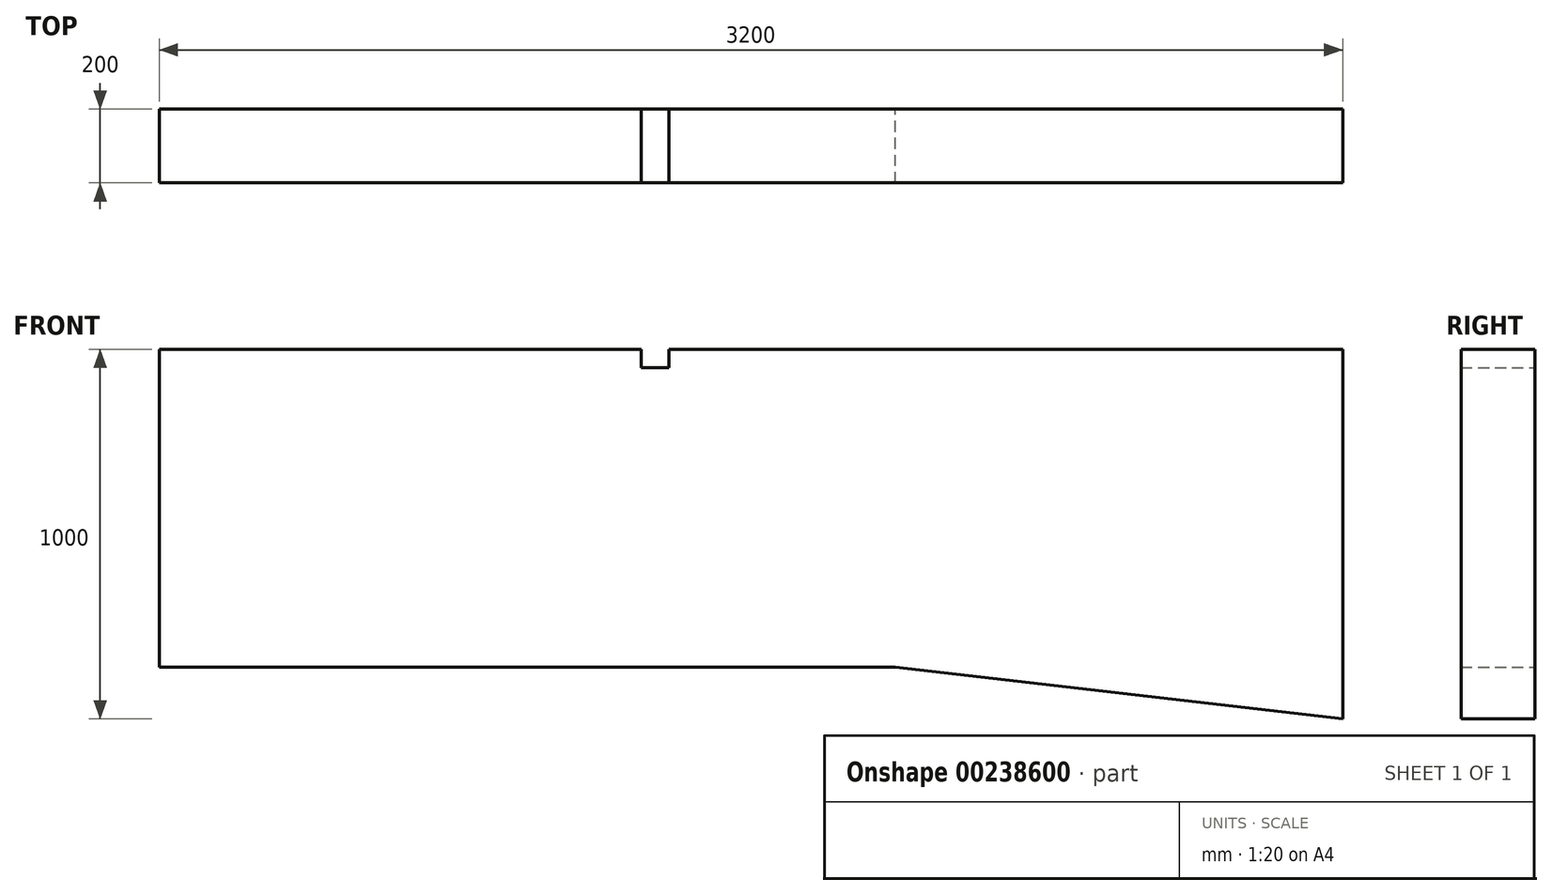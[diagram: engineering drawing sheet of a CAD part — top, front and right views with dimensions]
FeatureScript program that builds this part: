
annotation { "Feature Type Name" : "Feature", "Feature Type Description" : "" }
export const myFeature = defineFeature(function(context is Context, id is Id, definition is map)
    precondition{}
    {
        {
            var Q0;
            Q0=qCreatedBy(makeId("Front.planeOp"),FACE);
            var sketch = newSketch(context, id + "F0", { "sketchPlane" : qUnion([Q0])});
            skLineSegment(sketch, "E0.bottom", {"start": v(0, 0) * mm, "end": v(-3200, 0) * mm});
            skLineSegment(sketch, "E0.top", {"start": v(0, 860) * mm, "end": v(-3200, 860) * mm});
            skLineSegment(sketch, "E0.left", {"start": v(0, 0) * mm, "end": v(0, 860) * mm});
            skLineSegment(sketch, "E0.right", {"start": v(-3200, 0) * mm, "end": v(-3200, 860) * mm});
            skSolve(sketch);
        }
        {
            var Q0;
            Q0=makeQuery(id+"F0.imprint","IMPRINT",FACE,{"disambiguationData":[TD([[makeQuery(id+"F0.imprint","IMPRINT",EDGE,{"derivedFrom":sQuery(id+"F0.wireOp",EDGE,"E0.bottom")}),-1.0]])]});
            extrude(context, id + "F1", {"entities" : qUnion([Q0]), "depth" : 200 * mm});
        }
        {
            var Q0;
            Q0=qCreatedBy(makeId("Front.planeOp"),FACE);
            var sketch = newSketch(context, id + "F2", { "sketchPlane" : qUnion([Q0])});
            skLineSegment(sketch, "E1", {"start": v(0, 0) * mm, "end": v(0, -140) * mm});
            skLineSegment(sketch, "E2", {"start": v(0, -140) * mm, "end": v(-1210, 0) * mm});
            skLineSegment(sketch, "E3", {"start": v(-1210, 0) * mm, "end": v(0, 0) * mm});
            skSolve(sketch);
        }
        {
            var Q0;
            Q0=makeQuery(id+"F2.imprint","IMPRINT",FACE,{"disambiguationData":[TD([[makeQuery(id+"F2.imprint","IMPRINT",EDGE,{"derivedFrom":sQuery(id+"F2.wireOp",EDGE,"E1")}),-1.0]])]});
            var Q1;
            Q1=makeQuery(id+"F1.opExtrude","CAP_FACE",FACE,{"disambiguationData":[OSD([sQuery(id+"F0.wireOp",EDGE,"E0.bottom"),sQuery(id+"F0.wireOp",EDGE,"E0.top"),sQuery(id+"F0.wireOp",EDGE,"E0.left"),sQuery(id+"F0.wireOp",EDGE,"E0.right")])],"isStart":false});
            extrude(context, id + "F3", {"entities" : qUnion([Q0]), "operationType" : NewBodyOperationType.ADD, "endBound" : BoundingType.UP_TO_SURFACE, "endBoundEntityFace" : qUnion([Q1]), "depth" : 25 * mm});
        }
        {
            var Q0;
            Q0=qCreatedBy(makeId("Front.planeOp"),FACE);
            var sketch = newSketch(context, id + "F4", { "sketchPlane" : qUnion([Q0])});
            skLineSegment(sketch, "E4.bottom", {"start": v(-1897.5, 860) * mm, "end": v(-1822.5, 860) * mm});
            skLineSegment(sketch, "E4.top", {"start": v(-1897.5, 810) * mm, "end": v(-1822.5, 810) * mm});
            skLineSegment(sketch, "E4.left", {"start": v(-1897.5, 860) * mm, "end": v(-1897.5, 810) * mm});
            skLineSegment(sketch, "E4.right", {"start": v(-1822.5, 860) * mm, "end": v(-1822.5, 810) * mm});
            skSolve(sketch);
        }
        {
            var Q0;
            Q0 = qSketchRegion(id + "F4", true);
            extrude(context, id + "F5", {"entities" : qUnion([Q0]), "operationType" : NewBodyOperationType.REMOVE, "endBound" : BoundingType.THROUGH_ALL, "depth" : 25 * mm});
        }
    });
